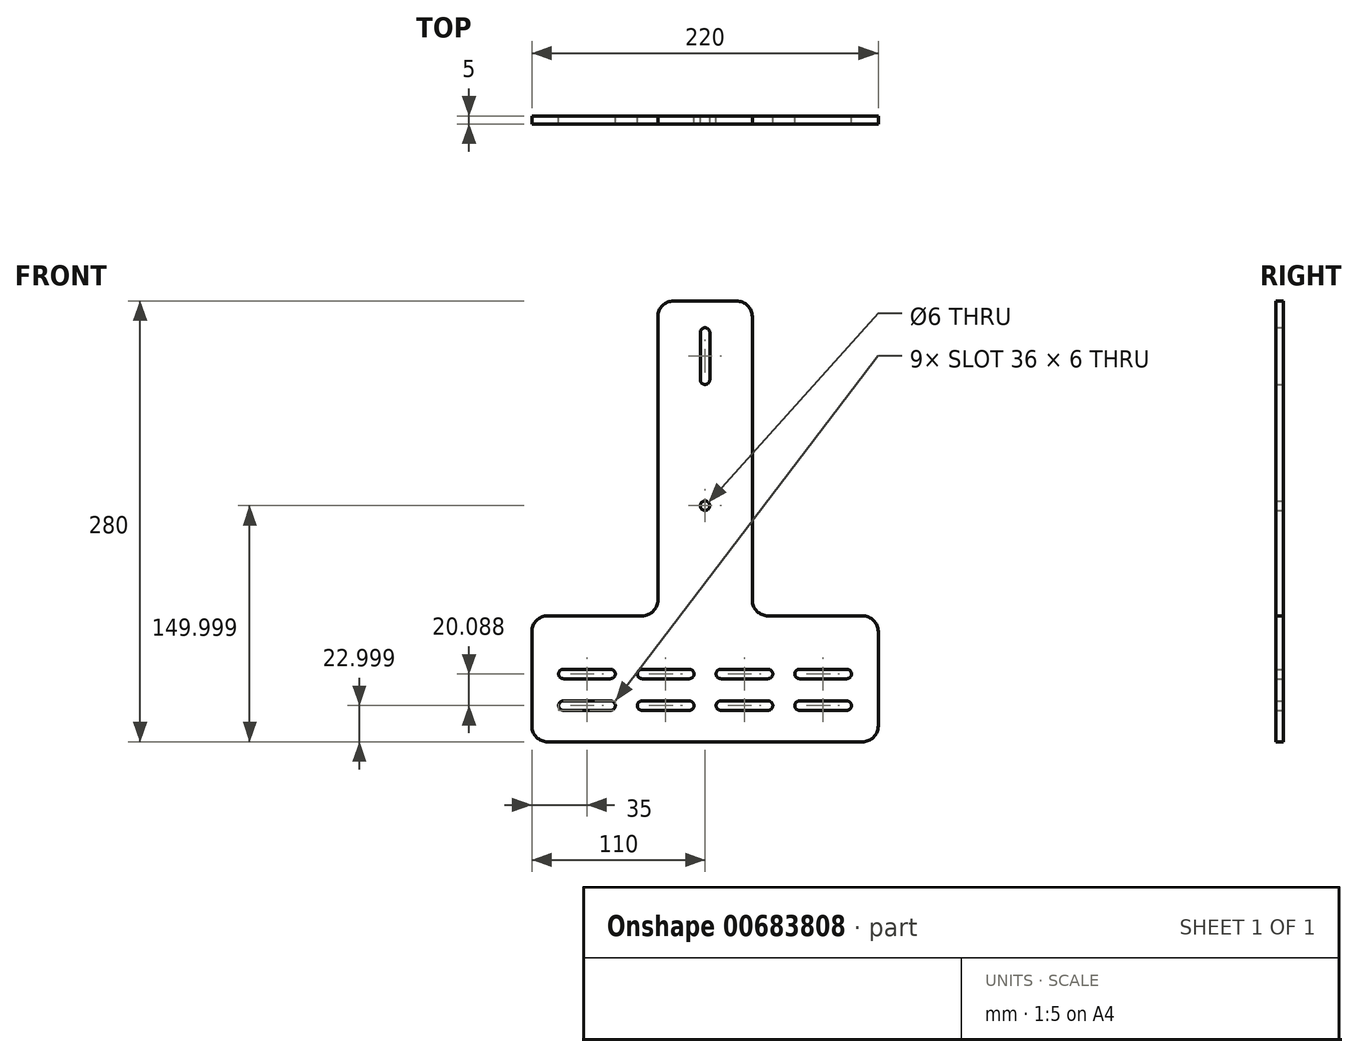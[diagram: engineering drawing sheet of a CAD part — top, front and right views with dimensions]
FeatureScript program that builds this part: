
annotation { "Feature Type Name" : "Feature", "Feature Type Description" : "" }
export const myFeature = defineFeature(function(context is Context, id is Id, definition is map)
    precondition{}
    {
        {
            var Q0;
            Q0=qCreatedBy(makeId("Front.planeOp"),FACE);
            var sketch = newSketch(context, id + "F0", { "sketchPlane" : qUnion([Q0])});
            skLineSegment(sketch, "E0.bottom", {"start": v(-100, -112.71) * mm, "end": v(100, -112.71) * mm});
            skLineSegment(sketch, "E0.top", {"start": v(-100, -32.71) * mm, "end": v(-40, -32.71) * mm});
            skLineSegment(sketch, "E0.left", {"start": v(-110, -102.71) * mm, "end": v(-110, -42.71) * mm});
            skLineSegment(sketch, "E0.right", {"start": v(110, -102.71) * mm, "end": v(110, -42.71) * mm});
            skLineSegment(sketch, "E1.bottom", {"start": v(-20, 167.29) * mm, "end": v(20, 167.29) * mm});
            skLineSegment(sketch, "E1.left", {"start": v(-30, 157.29) * mm, "end": v(-30, -22.71) * mm});
            skLineSegment(sketch, "E1.right", {"start": v(30, 157.29) * mm, "end": v(30, -22.71) * mm});
            skLineSegment(sketch, "E2.trimOffspring", {"start": v(40, -32.71) * mm, "end": v(100, -32.71) * mm});
            skPoint(sketch, "E3.visualSharp", {"position": v(-110, -32.71) * mm});
            skArc(sketch, "E3.filletArc", {"start": v(-100, -32.71) * mm, "mid": v(-107.07, -35.64) * mm, "end": v(-110, -42.71) * mm});
            skPoint(sketch, "E4.visualSharp", {"position": v(-110, -112.71) * mm});
            skArc(sketch, "E4.filletArc", {"start": v(-110, -102.71) * mm, "mid": v(-107.07, -109.78) * mm, "end": v(-100, -112.71) * mm});
            skPoint(sketch, "E5.visualSharp", {"position": v(110, -112.71) * mm});
            skArc(sketch, "E5.filletArc", {"start": v(100, -112.71) * mm, "mid": v(107.07, -109.78) * mm, "end": v(110, -102.71) * mm});
            skPoint(sketch, "E6.visualSharp", {"position": v(110, -32.71) * mm});
            skArc(sketch, "E6.filletArc", {"start": v(110, -42.71) * mm, "mid": v(107.07, -35.64) * mm, "end": v(100, -32.71) * mm});
            skPoint(sketch, "E7.visualSharp", {"position": v(30, -32.71) * mm});
            skArc(sketch, "E7.filletArc", {"start": v(30, -22.71) * mm, "mid": v(32.93, -29.78) * mm, "end": v(40, -32.71) * mm});
            skPoint(sketch, "E8.visualSharp", {"position": v(-30, -32.71) * mm});
            skArc(sketch, "E8.filletArc", {"start": v(-40, -32.71) * mm, "mid": v(-32.93, -29.78) * mm, "end": v(-30, -22.71) * mm});
            skPoint(sketch, "E9.visualSharp", {"position": v(-30, 167.29) * mm});
            skArc(sketch, "E9.filletArc", {"start": v(-20, 167.29) * mm, "mid": v(-27.07, 164.36) * mm, "end": v(-30, 157.29) * mm});
            skPoint(sketch, "E10.visualSharp", {"position": v(30, 167.29) * mm});
            skArc(sketch, "E10.filletArc", {"start": v(30, 157.29) * mm, "mid": v(27.07, 164.36) * mm, "end": v(20, 167.29) * mm});
            skCircle(sketch, "E11", {"center": v(0, 37.29) * mm, "radius": 3 * mm});
            skLineSegment(sketch, "E12.bottom", {"start": v(-90, -66.62) * mm, "end": v(-60, -66.62) * mm});
            skLineSegment(sketch, "E12.top", {"start": v(-90, -72.62) * mm, "end": v(-60, -72.62) * mm});
            skArc(sketch, "E13", {"start": v(-90, -66.62) * mm, "mid": v(-93, -69.62) * mm, "end": v(-90, -72.62) * mm});
            skArc(sketch, "E14", {"start": v(90, -72.62) * mm, "mid": v(93, -69.62) * mm, "end": v(90, -66.62) * mm});
            skLineSegment(sketch, "E15.trimOffspring", {"start": v(10, -72.62) * mm, "end": v(40, -72.62) * mm});
            skLineSegment(sketch, "E16.trimOffspring", {"start": v(10, -66.62) * mm, "end": v(40, -66.62) * mm});
            skArc(sketch, "E17", {"start": v(-10, -72.62) * mm, "mid": v(-7, -69.62) * mm, "end": v(-10, -66.62) * mm});
            skArc(sketch, "E18", {"start": v(10, -66.62) * mm, "mid": v(7, -69.62) * mm, "end": v(10, -72.62) * mm});
            skLineSegment(sketch, "E19.trimOffspring", {"start": v(-40, -66.62) * mm, "end": v(-10, -66.62) * mm});
            skLineSegment(sketch, "E20.trimOffspring", {"start": v(-40, -72.62) * mm, "end": v(-10, -72.62) * mm});
            skArc(sketch, "E21", {"start": v(-60, -72.62) * mm, "mid": v(-57, -69.62) * mm, "end": v(-60, -66.62) * mm});
            skArc(sketch, "E22", {"start": v(-40, -66.62) * mm, "mid": v(-43, -69.62) * mm, "end": v(-40, -72.62) * mm});
            skArc(sketch, "E23", {"start": v(40, -72.62) * mm, "mid": v(43, -69.62) * mm, "end": v(40, -66.62) * mm});
            skArc(sketch, "E24", {"start": v(60, -66.62) * mm, "mid": v(57, -69.62) * mm, "end": v(60, -72.62) * mm});
            skLineSegment(sketch, "E25.trimOffspring", {"start": v(60, -72.62) * mm, "end": v(90, -72.62) * mm});
            skLineSegment(sketch, "E26.trimOffspring", {"start": v(60, -66.62) * mm, "end": v(90, -66.62) * mm});
            skLineSegment(sketch, "E27.bottom", {"start": v(-90, -86.71) * mm, "end": v(-60, -86.71) * mm});
            skLineSegment(sketch, "E27.top", {"start": v(-90, -92.71) * mm, "end": v(-60, -92.71) * mm});
            skArc(sketch, "E28", {"start": v(-90, -86.71) * mm, "mid": v(-93, -89.71) * mm, "end": v(-90, -92.71) * mm});
            skArc(sketch, "E29", {"start": v(90, -92.71) * mm, "mid": v(93, -89.71) * mm, "end": v(90, -86.71) * mm});
            skLineSegment(sketch, "E30.trimOffspring", {"start": v(10, -92.71) * mm, "end": v(40, -92.71) * mm});
            skLineSegment(sketch, "E31.trimOffspring", {"start": v(10, -86.71) * mm, "end": v(40, -86.71) * mm});
            skArc(sketch, "E32", {"start": v(-10, -92.71) * mm, "mid": v(-7, -89.71) * mm, "end": v(-10, -86.71) * mm});
            skArc(sketch, "E33", {"start": v(10, -86.71) * mm, "mid": v(7, -89.71) * mm, "end": v(10, -92.71) * mm});
            skLineSegment(sketch, "E34.trimOffspring", {"start": v(-40, -86.71) * mm, "end": v(-10, -86.71) * mm});
            skLineSegment(sketch, "E35.trimOffspring", {"start": v(-40, -92.71) * mm, "end": v(-10, -92.71) * mm});
            skArc(sketch, "E36", {"start": v(-60, -92.71) * mm, "mid": v(-57, -89.71) * mm, "end": v(-60, -86.71) * mm});
            skArc(sketch, "E37", {"start": v(-40, -86.71) * mm, "mid": v(-43, -89.71) * mm, "end": v(-40, -92.71) * mm});
            skArc(sketch, "E38", {"start": v(40, -92.71) * mm, "mid": v(43, -89.71) * mm, "end": v(40, -86.71) * mm});
            skArc(sketch, "E39", {"start": v(60, -86.71) * mm, "mid": v(57, -89.71) * mm, "end": v(60, -92.71) * mm});
            skLineSegment(sketch, "E40.trimOffspring", {"start": v(60, -92.71) * mm, "end": v(90, -92.71) * mm});
            skLineSegment(sketch, "E41.trimOffspring", {"start": v(60, -86.71) * mm, "end": v(90, -86.71) * mm});
            skLineSegment(sketch, "E42.bottom", {"start": v(3, 147.29) * mm, "end": v(3, 117.29) * mm});
            skLineSegment(sketch, "E42.top", {"start": v(-3, 147.29) * mm, "end": v(-3, 117.29) * mm});
            skArc(sketch, "E43", {"start": v(3, 147.29) * mm, "mid": v(0, 150.29) * mm, "end": v(-3, 147.29) * mm});
            skArc(sketch, "E44", {"start": v(-3, 117.29) * mm, "mid": v(0, 114.29) * mm, "end": v(3, 117.29) * mm});
            skSolve(sketch);
        }
        {
            var Q0;
            Q0 = qSketchRegion(id + "F0", true);
            extrude(context, id + "F1", {"entities" : qUnion([Q0]), "depth" : 5 * mm, "offsetDistance" : 25 * mm});
        }
    });
